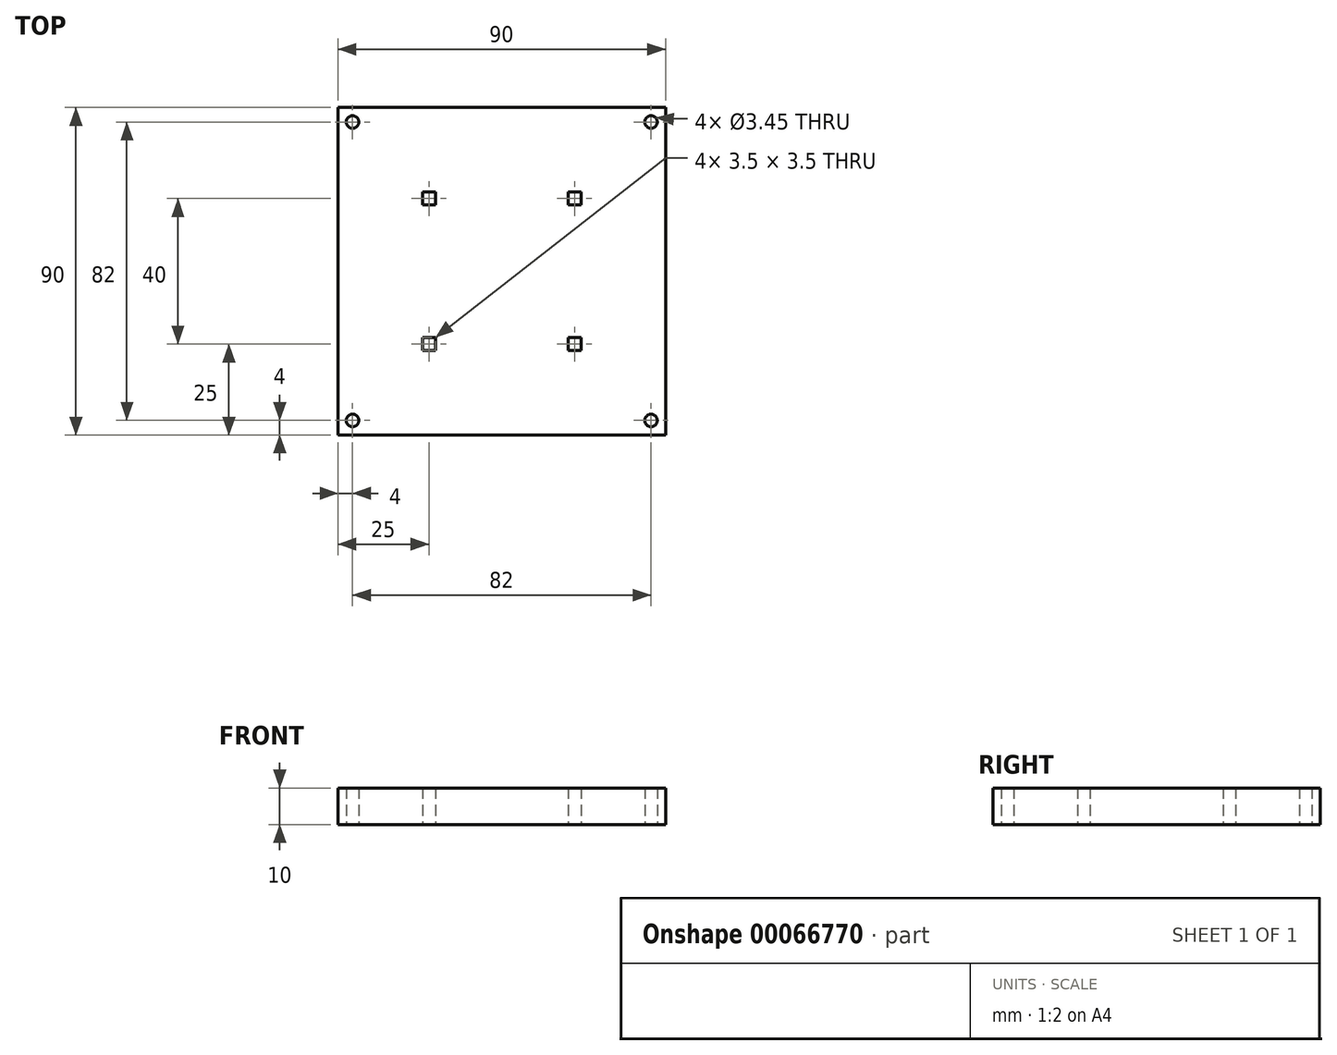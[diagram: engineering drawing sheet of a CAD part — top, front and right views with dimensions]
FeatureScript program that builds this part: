
annotation { "Feature Type Name" : "Feature", "Feature Type Description" : "" }
export const myFeature = defineFeature(function(context is Context, id is Id, definition is map)
    precondition{}
    {
        {
            var Q0;
            Q0=qCreatedBy(makeId("Top.planeOp"),FACE);
            var sketch = newSketch(context, id + "F0", { "sketchPlane" : qUnion([Q0])});
            skLineSegment(sketch, "E0", {"start": v(45, 0) * mm, "end": v(45, 45) * mm});
            skLineSegment(sketch, "E1", {"start": v(45, 45) * mm, "end": v(0, 45) * mm});
            skLineSegment(sketch, "E2", {"start": v(41, 41) * mm, "end": v(41, 45) * mm, "construction": true});
            skLineSegment(sketch, "E3", {"start": v(41, 41) * mm, "end": v(45, 41) * mm, "construction": true});
            skCircle(sketch, "E4", {"center": v(41, 41) * mm, "radius": 1.73 * mm});
            skLineSegment(sketch, "E5.MirrorCS", {"start": v(-41, 41) * mm, "end": v(-45, 41) * mm, "construction": true});
            skLineSegment(sketch, "E6.MirrorCS", {"start": v(-41, 41) * mm, "end": v(-41, 45) * mm, "construction": true});
            skCircle(sketch, "E7.MirrorC", {"center": v(-41, 41) * mm, "radius": 1.73 * mm});
            skLineSegment(sketch, "E8.MirrorCS", {"start": v(-45, 45) * mm, "end": v(0, 45) * mm});
            skLineSegment(sketch, "E9.MirrorCS", {"start": v(-45, 0) * mm, "end": v(-45, 45) * mm});
            skCircle(sketch, "E10.MirrorC", {"center": v(-41, -41) * mm, "radius": 1.73 * mm});
            skLineSegment(sketch, "E11.MirrorCS", {"start": v(-41, -41) * mm, "end": v(-41, -45) * mm, "construction": true});
            skLineSegment(sketch, "E12.MirrorCS", {"start": v(41, -41) * mm, "end": v(45, -41) * mm, "construction": true});
            skLineSegment(sketch, "E13.MirrorCS", {"start": v(41, -41) * mm, "end": v(41, -45) * mm, "construction": true});
            skLineSegment(sketch, "E14.MirrorCS", {"start": v(-41, -41) * mm, "end": v(-45, -41) * mm, "construction": true});
            skLineSegment(sketch, "E15.MirrorCS", {"start": v(-45, 0) * mm, "end": v(-45, -45) * mm});
            skLineSegment(sketch, "E16.MirrorCS", {"start": v(-45, -45) * mm, "end": v(0, -45) * mm});
            skLineSegment(sketch, "E17.MirrorCS", {"start": v(45, 0) * mm, "end": v(45, -45) * mm});
            skLineSegment(sketch, "E18.MirrorCS", {"start": v(45, -45) * mm, "end": v(0, -45) * mm});
            skCircle(sketch, "E19.MirrorC", {"center": v(41, -41) * mm, "radius": 1.73 * mm});
            skLineSegment(sketch, "E20", {"start": v(45, -20) * mm, "end": v(20, -20) * mm, "construction": true});
            skLineSegment(sketch, "E21", {"start": v(20, -20) * mm, "end": v(-20, -20) * mm, "construction": true});
            skLineSegment(sketch, "E22", {"start": v(-20, -20) * mm, "end": v(-45, -20) * mm, "construction": true});
            skLineSegment(sketch, "E23", {"start": v(-20, -20) * mm, "end": v(-20, 20) * mm, "construction": true});
            skLineSegment(sketch, "E24", {"start": v(-20, 20) * mm, "end": v(20, 20) * mm, "construction": true});
            skLineSegment(sketch, "E25", {"start": v(20, 20) * mm, "end": v(20, -20) * mm, "construction": true});
            skLineSegment(sketch, "E26.rect.bottom", {"start": v(-18.25, 18.25) * mm, "end": v(-21.75, 18.25) * mm});
            skLineSegment(sketch, "E26.rect.top", {"start": v(-18.25, 21.75) * mm, "end": v(-21.75, 21.75) * mm});
            skLineSegment(sketch, "E26.rect.left", {"start": v(-18.25, 18.25) * mm, "end": v(-18.25, 21.75) * mm});
            skLineSegment(sketch, "E26.rect.right", {"start": v(-21.75, 18.25) * mm, "end": v(-21.75, 21.75) * mm});
            skPoint(sketch, "E26.rect.middle", {"position": v(-20, 20) * mm});
            skLineSegment(sketch, "E27.MirrorCS", {"start": v(18.25, 18.25) * mm, "end": v(18.25, 21.75) * mm});
            skLineSegment(sketch, "E28.MirrorCS", {"start": v(18.25, 21.75) * mm, "end": v(21.75, 21.75) * mm});
            skLineSegment(sketch, "E29.MirrorCS", {"start": v(18.25, 18.25) * mm, "end": v(21.75, 18.25) * mm});
            skLineSegment(sketch, "E30.MirrorCS", {"start": v(21.75, 18.25) * mm, "end": v(21.75, 21.75) * mm});
            skLineSegment(sketch, "E31.MirrorCS", {"start": v(-18.25, -21.75) * mm, "end": v(-21.75, -21.75) * mm});
            skLineSegment(sketch, "E32.MirrorCS", {"start": v(-21.75, -18.25) * mm, "end": v(-21.75, -21.75) * mm});
            skLineSegment(sketch, "E33.MirrorCS", {"start": v(-18.25, -18.25) * mm, "end": v(-21.75, -18.25) * mm});
            skLineSegment(sketch, "E34.MirrorCS", {"start": v(-18.25, -18.25) * mm, "end": v(-18.25, -21.75) * mm});
            skLineSegment(sketch, "E35.MirrorCS", {"start": v(18.25, -18.25) * mm, "end": v(18.25, -21.75) * mm});
            skLineSegment(sketch, "E36.MirrorCS", {"start": v(18.25, -18.25) * mm, "end": v(21.75, -18.25) * mm});
            skLineSegment(sketch, "E37.MirrorCS", {"start": v(18.25, -21.75) * mm, "end": v(21.75, -21.75) * mm});
            skLineSegment(sketch, "E38.MirrorCS", {"start": v(21.75, -18.25) * mm, "end": v(21.75, -21.75) * mm});
            skSolve(sketch);
        }
        {
            var Q0;
            Q0=qSketchRegion(id+"F0",true);
            extrude(context, id + "F1", {"entities" : qUnion([Q0]), "depth" : 10 * mm});
        }
    });
